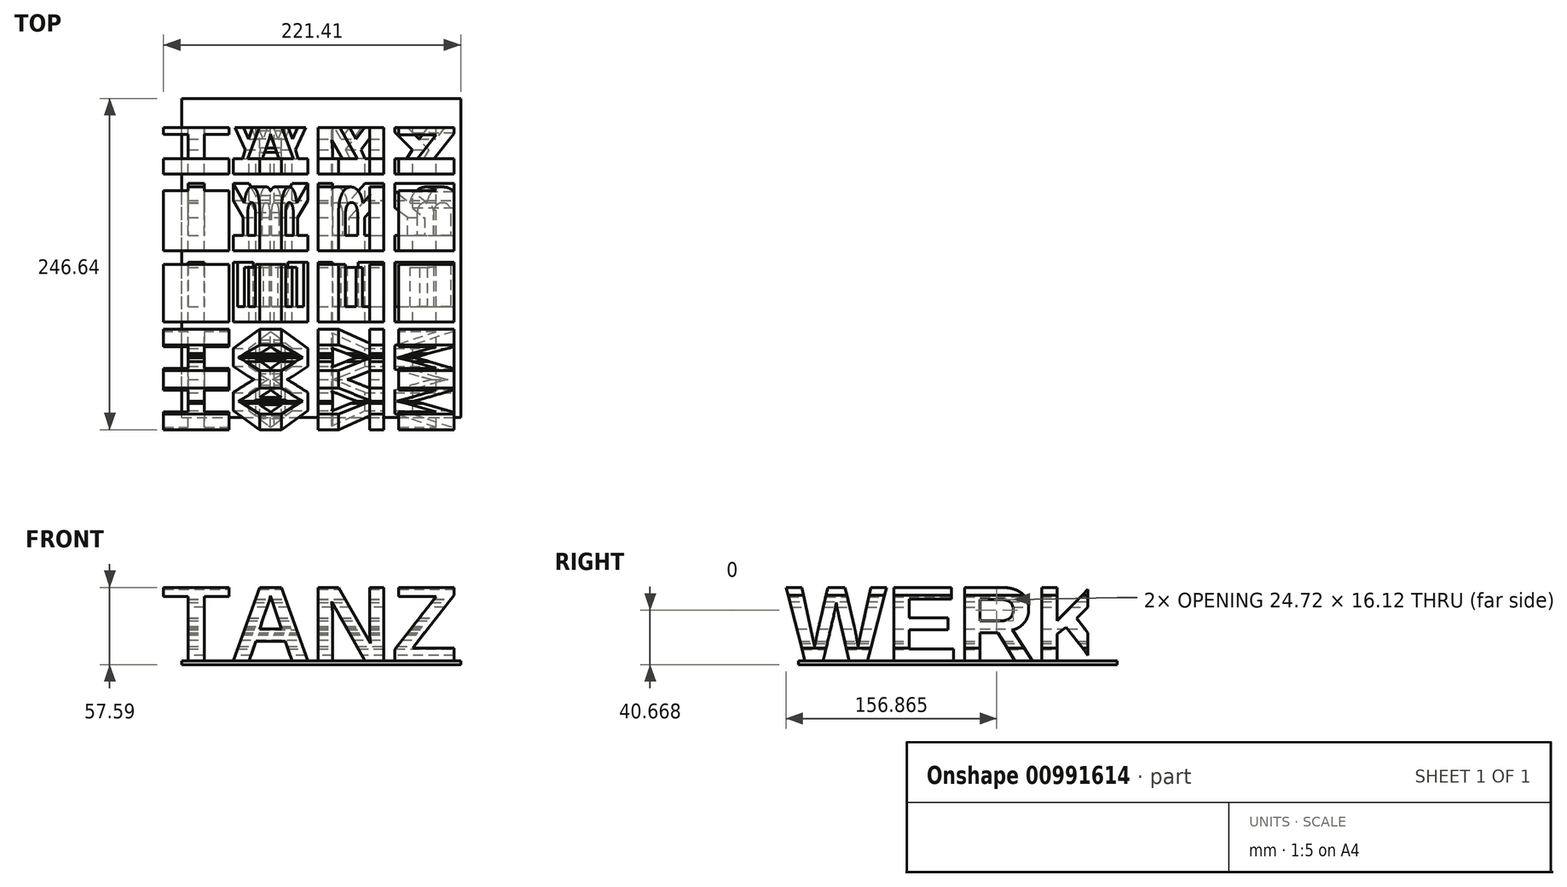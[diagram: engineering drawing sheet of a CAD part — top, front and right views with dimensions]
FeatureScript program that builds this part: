
annotation { "Feature Type Name" : "Feature", "Feature Type Description" : "" }
export const myFeature = defineFeature(function(context is Context, id is Id, definition is map)
    precondition{}
    {
        {
            var Q0;
            Q0=qCreatedBy(makeId("Front.planeOp"),FACE);
            var sketch = newSketch(context, id + "F0", { "sketchPlane" : qUnion([Q0])});
            skText(sketch, "E0", { "text": "TANZ", "fontName": "Arimo-Bold.ttf"});
            const initialGuessF0  = {"E0": [-0.14984, 0, 1, 0, 0.03986]};
            skSetInitialGuess(sketch, initialGuessF0);
            skSolve(sketch);
        }
        {
            var Q0;
            Q0 = qSketchRegion(id + "F0", true);
            extrude(context, id + "F1", {"entities" : qUnion([Q0]), "depth" : 164.8 * mm, "offsetDistance" : 25 * mm});
        }
        {
            var Q0;
            Q0=makeQuery(id+"F1.opExtrude","SWEPT_FACE",FACE,{"disambiguationData":[OSD([sQuery(id+"F0.wireOp",EDGE,"E0.sketch_text.stroke-41")])]});
            var sketch = newSketch(context, id + "F2", { "sketchPlane" : qUnion([Q0])});
            skPoint(sketch, "E1.0", {"position": v(-164.8, 38.09) * mm});
            skPoint(sketch, "E2.0", {"position": v(0, 0) * mm});
            skText(sketch, "E3", { "text": "WERK", "fontName": "Arimo-Bold.ttf"});
            const initialGuessF2  = {"E3": [-0.15, 0, 1, 0, 0.03809]};
            skSetInitialGuess(sketch, initialGuessF2);
            skSolve(sketch);
        }
        {
            var Q0;
            Q0 = qSketchRegion(id + "F2", true);
            extrude(context, id + "F3", {"entities" : qUnion([Q0]), "operationType" : NewBodyOperationType.INTERSECT, "endBound" : BoundingType.THROUGH_ALL, "oppositeDirection" : true, "depth" : 25 * mm, "offsetDistance" : 25 * mm});
        }
        {
            var Q0;
            Q0=makeQuery(id+"F3.boolean.opBoolean","SPLIT",BODY,{"disambiguationData":[OD(0.0)],"derivedFrom":makeQuery(id+"F1.opExtrude","SWEPT_BODY",BODY,{"disambiguationData":[OSD([sQuery(id+"F0.wireOp",EDGE,"E0.sketch_text.stroke-0"),sQuery(id+"F0.wireOp",EDGE,"E0.sketch_text.stroke-1"),sQuery(id+"F0.wireOp",EDGE,"E0.sketch_text.stroke-2"),sQuery(id+"F0.wireOp",EDGE,"E0.sketch_text.stroke-3"),sQuery(id+"F0.wireOp",EDGE,"E0.sketch_text.stroke-4"),sQuery(id+"F0.wireOp",EDGE,"E0.sketch_text.stroke-5"),sQuery(id+"F0.wireOp",EDGE,"E0.sketch_text.stroke-6"),sQuery(id+"F0.wireOp",EDGE,"E0.sketch_text.stroke-7")])]})});
            var Q1;
            Q1=makeQuery(id+"F3.boolean.opBoolean","SPLIT",BODY,{"disambiguationData":[OD(1.0)],"derivedFrom":makeQuery(id+"F1.opExtrude","SWEPT_BODY",BODY,{"disambiguationData":[OSD([sQuery(id+"F0.wireOp",EDGE,"E0.sketch_text.stroke-0"),sQuery(id+"F0.wireOp",EDGE,"E0.sketch_text.stroke-1"),sQuery(id+"F0.wireOp",EDGE,"E0.sketch_text.stroke-2"),sQuery(id+"F0.wireOp",EDGE,"E0.sketch_text.stroke-3"),sQuery(id+"F0.wireOp",EDGE,"E0.sketch_text.stroke-4"),sQuery(id+"F0.wireOp",EDGE,"E0.sketch_text.stroke-5"),sQuery(id+"F0.wireOp",EDGE,"E0.sketch_text.stroke-6"),sQuery(id+"F0.wireOp",EDGE,"E0.sketch_text.stroke-7")])]})});
            var Q2;
            Q2=makeQuery(id+"F3.boolean.opBoolean","SPLIT",BODY,{"disambiguationData":[OD(2.0)],"derivedFrom":makeQuery(id+"F1.opExtrude","SWEPT_BODY",BODY,{"disambiguationData":[OSD([sQuery(id+"F0.wireOp",EDGE,"E0.sketch_text.stroke-0"),sQuery(id+"F0.wireOp",EDGE,"E0.sketch_text.stroke-1"),sQuery(id+"F0.wireOp",EDGE,"E0.sketch_text.stroke-2"),sQuery(id+"F0.wireOp",EDGE,"E0.sketch_text.stroke-3"),sQuery(id+"F0.wireOp",EDGE,"E0.sketch_text.stroke-4"),sQuery(id+"F0.wireOp",EDGE,"E0.sketch_text.stroke-5"),sQuery(id+"F0.wireOp",EDGE,"E0.sketch_text.stroke-6"),sQuery(id+"F0.wireOp",EDGE,"E0.sketch_text.stroke-7")])]})});
            var Q3;
            Q3=makeQuery(id+"F3.boolean.opBoolean","SPLIT",BODY,{"disambiguationData":[OD(3.0)],"derivedFrom":makeQuery(id+"F1.opExtrude","SWEPT_BODY",BODY,{"disambiguationData":[OSD([sQuery(id+"F0.wireOp",EDGE,"E0.sketch_text.stroke-0"),sQuery(id+"F0.wireOp",EDGE,"E0.sketch_text.stroke-1"),sQuery(id+"F0.wireOp",EDGE,"E0.sketch_text.stroke-2"),sQuery(id+"F0.wireOp",EDGE,"E0.sketch_text.stroke-3"),sQuery(id+"F0.wireOp",EDGE,"E0.sketch_text.stroke-4"),sQuery(id+"F0.wireOp",EDGE,"E0.sketch_text.stroke-5"),sQuery(id+"F0.wireOp",EDGE,"E0.sketch_text.stroke-6"),sQuery(id+"F0.wireOp",EDGE,"E0.sketch_text.stroke-7")])]})});
            var Q4;
            Q4=makeQuery(id+"F3.boolean.opBoolean","SPLIT",BODY,{"disambiguationData":[OD(0.0)],"derivedFrom":makeQuery(id+"F1.opExtrude","SWEPT_BODY",BODY,{"disambiguationData":[OSD([sQuery(id+"F0.wireOp",EDGE,"E0.sketch_text.stroke-8"),sQuery(id+"F0.wireOp",EDGE,"E0.sketch_text.stroke-9"),sQuery(id+"F0.wireOp",EDGE,"E0.sketch_text.stroke-10"),sQuery(id+"F0.wireOp",EDGE,"E0.sketch_text.stroke-11"),sQuery(id+"F0.wireOp",EDGE,"E0.sketch_text.stroke-12"),sQuery(id+"F0.wireOp",EDGE,"E0.sketch_text.stroke-13"),sQuery(id+"F0.wireOp",EDGE,"E0.sketch_text.stroke-14"),sQuery(id+"F0.wireOp",EDGE,"E0.sketch_text.stroke-15"),sQuery(id+"F0.wireOp",EDGE,"E0.sketch_text.stroke-16"),sQuery(id+"F0.wireOp",EDGE,"E0.sketch_text.stroke-17"),sQuery(id+"F0.wireOp",EDGE,"E0.sketch_text.stroke-18"),sQuery(id+"F0.wireOp",EDGE,"E0.sketch_text.stroke-19"),sQuery(id+"F0.wireOp",EDGE,"E0.sketch_text.stroke-20"),sQuery(id+"F0.wireOp",EDGE,"E0.sketch_text.stroke-21"),sQuery(id+"F0.wireOp",EDGE,"E0.sketch_text.stroke-22")])]})});
            var Q5;
            Q5=makeQuery(id+"F3.boolean.opBoolean","SPLIT",BODY,{"disambiguationData":[OD(1.0)],"derivedFrom":makeQuery(id+"F1.opExtrude","SWEPT_BODY",BODY,{"disambiguationData":[OSD([sQuery(id+"F0.wireOp",EDGE,"E0.sketch_text.stroke-8"),sQuery(id+"F0.wireOp",EDGE,"E0.sketch_text.stroke-9"),sQuery(id+"F0.wireOp",EDGE,"E0.sketch_text.stroke-10"),sQuery(id+"F0.wireOp",EDGE,"E0.sketch_text.stroke-11"),sQuery(id+"F0.wireOp",EDGE,"E0.sketch_text.stroke-12"),sQuery(id+"F0.wireOp",EDGE,"E0.sketch_text.stroke-13"),sQuery(id+"F0.wireOp",EDGE,"E0.sketch_text.stroke-14"),sQuery(id+"F0.wireOp",EDGE,"E0.sketch_text.stroke-15"),sQuery(id+"F0.wireOp",EDGE,"E0.sketch_text.stroke-16"),sQuery(id+"F0.wireOp",EDGE,"E0.sketch_text.stroke-17"),sQuery(id+"F0.wireOp",EDGE,"E0.sketch_text.stroke-18"),sQuery(id+"F0.wireOp",EDGE,"E0.sketch_text.stroke-19"),sQuery(id+"F0.wireOp",EDGE,"E0.sketch_text.stroke-20"),sQuery(id+"F0.wireOp",EDGE,"E0.sketch_text.stroke-21"),sQuery(id+"F0.wireOp",EDGE,"E0.sketch_text.stroke-22")])]})});
            var Q6;
            Q6=makeQuery(id+"F3.boolean.opBoolean","SPLIT",BODY,{"disambiguationData":[OD(2.0)],"derivedFrom":makeQuery(id+"F1.opExtrude","SWEPT_BODY",BODY,{"disambiguationData":[OSD([sQuery(id+"F0.wireOp",EDGE,"E0.sketch_text.stroke-8"),sQuery(id+"F0.wireOp",EDGE,"E0.sketch_text.stroke-9"),sQuery(id+"F0.wireOp",EDGE,"E0.sketch_text.stroke-10"),sQuery(id+"F0.wireOp",EDGE,"E0.sketch_text.stroke-11"),sQuery(id+"F0.wireOp",EDGE,"E0.sketch_text.stroke-12"),sQuery(id+"F0.wireOp",EDGE,"E0.sketch_text.stroke-13"),sQuery(id+"F0.wireOp",EDGE,"E0.sketch_text.stroke-14"),sQuery(id+"F0.wireOp",EDGE,"E0.sketch_text.stroke-15"),sQuery(id+"F0.wireOp",EDGE,"E0.sketch_text.stroke-16"),sQuery(id+"F0.wireOp",EDGE,"E0.sketch_text.stroke-17"),sQuery(id+"F0.wireOp",EDGE,"E0.sketch_text.stroke-18"),sQuery(id+"F0.wireOp",EDGE,"E0.sketch_text.stroke-19"),sQuery(id+"F0.wireOp",EDGE,"E0.sketch_text.stroke-20"),sQuery(id+"F0.wireOp",EDGE,"E0.sketch_text.stroke-21"),sQuery(id+"F0.wireOp",EDGE,"E0.sketch_text.stroke-22")])]})});
            var Q7;
            Q7=makeQuery(id+"F3.boolean.opBoolean","SPLIT",BODY,{"disambiguationData":[OD(3.0)],"derivedFrom":makeQuery(id+"F1.opExtrude","SWEPT_BODY",BODY,{"disambiguationData":[OSD([sQuery(id+"F0.wireOp",EDGE,"E0.sketch_text.stroke-8"),sQuery(id+"F0.wireOp",EDGE,"E0.sketch_text.stroke-9"),sQuery(id+"F0.wireOp",EDGE,"E0.sketch_text.stroke-10"),sQuery(id+"F0.wireOp",EDGE,"E0.sketch_text.stroke-11"),sQuery(id+"F0.wireOp",EDGE,"E0.sketch_text.stroke-12"),sQuery(id+"F0.wireOp",EDGE,"E0.sketch_text.stroke-13"),sQuery(id+"F0.wireOp",EDGE,"E0.sketch_text.stroke-14"),sQuery(id+"F0.wireOp",EDGE,"E0.sketch_text.stroke-15"),sQuery(id+"F0.wireOp",EDGE,"E0.sketch_text.stroke-16"),sQuery(id+"F0.wireOp",EDGE,"E0.sketch_text.stroke-17"),sQuery(id+"F0.wireOp",EDGE,"E0.sketch_text.stroke-18"),sQuery(id+"F0.wireOp",EDGE,"E0.sketch_text.stroke-19"),sQuery(id+"F0.wireOp",EDGE,"E0.sketch_text.stroke-20"),sQuery(id+"F0.wireOp",EDGE,"E0.sketch_text.stroke-21"),sQuery(id+"F0.wireOp",EDGE,"E0.sketch_text.stroke-22")])]})});
            var Q8;
            Q8=makeQuery(id+"F3.boolean.opBoolean","SPLIT",BODY,{"disambiguationData":[OD(0.0)],"derivedFrom":makeQuery(id+"F1.opExtrude","SWEPT_BODY",BODY,{"disambiguationData":[OSD([sQuery(id+"F0.wireOp",EDGE,"E0.sketch_text.stroke-23"),sQuery(id+"F0.wireOp",EDGE,"E0.sketch_text.stroke-24"),sQuery(id+"F0.wireOp",EDGE,"E0.sketch_text.stroke-25"),sQuery(id+"F0.wireOp",EDGE,"E0.sketch_text.stroke-26"),sQuery(id+"F0.wireOp",EDGE,"E0.sketch_text.stroke-27"),sQuery(id+"F0.wireOp",EDGE,"E0.sketch_text.stroke-28"),sQuery(id+"F0.wireOp",EDGE,"E0.sketch_text.stroke-29"),sQuery(id+"F0.wireOp",EDGE,"E0.sketch_text.stroke-30"),sQuery(id+"F0.wireOp",EDGE,"E0.sketch_text.stroke-31"),sQuery(id+"F0.wireOp",EDGE,"E0.sketch_text.stroke-32"),sQuery(id+"F0.wireOp",EDGE,"E0.sketch_text.stroke-33"),sQuery(id+"F0.wireOp",EDGE,"E0.sketch_text.stroke-34")])]})});
            var Q9;
            Q9=makeQuery(id+"F3.boolean.opBoolean","SPLIT",BODY,{"disambiguationData":[OD(1.0)],"derivedFrom":makeQuery(id+"F1.opExtrude","SWEPT_BODY",BODY,{"disambiguationData":[OSD([sQuery(id+"F0.wireOp",EDGE,"E0.sketch_text.stroke-23"),sQuery(id+"F0.wireOp",EDGE,"E0.sketch_text.stroke-24"),sQuery(id+"F0.wireOp",EDGE,"E0.sketch_text.stroke-25"),sQuery(id+"F0.wireOp",EDGE,"E0.sketch_text.stroke-26"),sQuery(id+"F0.wireOp",EDGE,"E0.sketch_text.stroke-27"),sQuery(id+"F0.wireOp",EDGE,"E0.sketch_text.stroke-28"),sQuery(id+"F0.wireOp",EDGE,"E0.sketch_text.stroke-29"),sQuery(id+"F0.wireOp",EDGE,"E0.sketch_text.stroke-30"),sQuery(id+"F0.wireOp",EDGE,"E0.sketch_text.stroke-31"),sQuery(id+"F0.wireOp",EDGE,"E0.sketch_text.stroke-32"),sQuery(id+"F0.wireOp",EDGE,"E0.sketch_text.stroke-33"),sQuery(id+"F0.wireOp",EDGE,"E0.sketch_text.stroke-34")])]})});
            var Q10;
            Q10=makeQuery(id+"F3.boolean.opBoolean","SPLIT",BODY,{"disambiguationData":[OD(0.0)],"derivedFrom":makeQuery(id+"F1.opExtrude","SWEPT_BODY",BODY,{"disambiguationData":[OSD([sQuery(id+"F0.wireOp",EDGE,"E0.sketch_text.stroke-35"),sQuery(id+"F0.wireOp",EDGE,"E0.sketch_text.stroke-36"),sQuery(id+"F0.wireOp",EDGE,"E0.sketch_text.stroke-37"),sQuery(id+"F0.wireOp",EDGE,"E0.sketch_text.stroke-38"),sQuery(id+"F0.wireOp",EDGE,"E0.sketch_text.stroke-39"),sQuery(id+"F0.wireOp",EDGE,"E0.sketch_text.stroke-40"),sQuery(id+"F0.wireOp",EDGE,"E0.sketch_text.stroke-41"),sQuery(id+"F0.wireOp",EDGE,"E0.sketch_text.stroke-42"),sQuery(id+"F0.wireOp",EDGE,"E0.sketch_text.stroke-43"),sQuery(id+"F0.wireOp",EDGE,"E0.sketch_text.stroke-44")])]})});
            var Q11;
            Q11=makeQuery(id+"F3.boolean.opBoolean","SPLIT",BODY,{"disambiguationData":[OD(1.0)],"derivedFrom":makeQuery(id+"F1.opExtrude","SWEPT_BODY",BODY,{"disambiguationData":[OSD([sQuery(id+"F0.wireOp",EDGE,"E0.sketch_text.stroke-35"),sQuery(id+"F0.wireOp",EDGE,"E0.sketch_text.stroke-36"),sQuery(id+"F0.wireOp",EDGE,"E0.sketch_text.stroke-37"),sQuery(id+"F0.wireOp",EDGE,"E0.sketch_text.stroke-38"),sQuery(id+"F0.wireOp",EDGE,"E0.sketch_text.stroke-39"),sQuery(id+"F0.wireOp",EDGE,"E0.sketch_text.stroke-40"),sQuery(id+"F0.wireOp",EDGE,"E0.sketch_text.stroke-41"),sQuery(id+"F0.wireOp",EDGE,"E0.sketch_text.stroke-42"),sQuery(id+"F0.wireOp",EDGE,"E0.sketch_text.stroke-43"),sQuery(id+"F0.wireOp",EDGE,"E0.sketch_text.stroke-44")])]})});
            var Q12;
            Q12=makeQuery(id+"F3.boolean.opBoolean","SPLIT",BODY,{"disambiguationData":[OD(2.0)],"derivedFrom":makeQuery(id+"F1.opExtrude","SWEPT_BODY",BODY,{"disambiguationData":[OSD([sQuery(id+"F0.wireOp",EDGE,"E0.sketch_text.stroke-35"),sQuery(id+"F0.wireOp",EDGE,"E0.sketch_text.stroke-36"),sQuery(id+"F0.wireOp",EDGE,"E0.sketch_text.stroke-37"),sQuery(id+"F0.wireOp",EDGE,"E0.sketch_text.stroke-38"),sQuery(id+"F0.wireOp",EDGE,"E0.sketch_text.stroke-39"),sQuery(id+"F0.wireOp",EDGE,"E0.sketch_text.stroke-40"),sQuery(id+"F0.wireOp",EDGE,"E0.sketch_text.stroke-41"),sQuery(id+"F0.wireOp",EDGE,"E0.sketch_text.stroke-42"),sQuery(id+"F0.wireOp",EDGE,"E0.sketch_text.stroke-43"),sQuery(id+"F0.wireOp",EDGE,"E0.sketch_text.stroke-44")])]})});
            var Q13;
            Q13=makeQuery(id+"F3.boolean.opBoolean","SPLIT",BODY,{"disambiguationData":[OD(3.0)],"derivedFrom":makeQuery(id+"F1.opExtrude","SWEPT_BODY",BODY,{"disambiguationData":[OSD([sQuery(id+"F0.wireOp",EDGE,"E0.sketch_text.stroke-35"),sQuery(id+"F0.wireOp",EDGE,"E0.sketch_text.stroke-36"),sQuery(id+"F0.wireOp",EDGE,"E0.sketch_text.stroke-37"),sQuery(id+"F0.wireOp",EDGE,"E0.sketch_text.stroke-38"),sQuery(id+"F0.wireOp",EDGE,"E0.sketch_text.stroke-39"),sQuery(id+"F0.wireOp",EDGE,"E0.sketch_text.stroke-40"),sQuery(id+"F0.wireOp",EDGE,"E0.sketch_text.stroke-41"),sQuery(id+"F0.wireOp",EDGE,"E0.sketch_text.stroke-42"),sQuery(id+"F0.wireOp",EDGE,"E0.sketch_text.stroke-43"),sQuery(id+"F0.wireOp",EDGE,"E0.sketch_text.stroke-44")])]})});
            var Q14;
            Q14=makeQuery(id+"F3.boolean.opBoolean","SPLIT",BODY,{"disambiguationData":[OD(2.0)],"derivedFrom":makeQuery(id+"F1.opExtrude","SWEPT_BODY",BODY,{"disambiguationData":[OSD([sQuery(id+"F0.wireOp",EDGE,"E0.sketch_text.stroke-23"),sQuery(id+"F0.wireOp",EDGE,"E0.sketch_text.stroke-24"),sQuery(id+"F0.wireOp",EDGE,"E0.sketch_text.stroke-25"),sQuery(id+"F0.wireOp",EDGE,"E0.sketch_text.stroke-26"),sQuery(id+"F0.wireOp",EDGE,"E0.sketch_text.stroke-27"),sQuery(id+"F0.wireOp",EDGE,"E0.sketch_text.stroke-28"),sQuery(id+"F0.wireOp",EDGE,"E0.sketch_text.stroke-29"),sQuery(id+"F0.wireOp",EDGE,"E0.sketch_text.stroke-30"),sQuery(id+"F0.wireOp",EDGE,"E0.sketch_text.stroke-31"),sQuery(id+"F0.wireOp",EDGE,"E0.sketch_text.stroke-32"),sQuery(id+"F0.wireOp",EDGE,"E0.sketch_text.stroke-33"),sQuery(id+"F0.wireOp",EDGE,"E0.sketch_text.stroke-34")])]})});
            var Q15;
            Q15=makeQuery(id+"F3.boolean.opBoolean","SPLIT",BODY,{"disambiguationData":[OD(3.0)],"derivedFrom":makeQuery(id+"F1.opExtrude","SWEPT_BODY",BODY,{"disambiguationData":[OSD([sQuery(id+"F0.wireOp",EDGE,"E0.sketch_text.stroke-23"),sQuery(id+"F0.wireOp",EDGE,"E0.sketch_text.stroke-24"),sQuery(id+"F0.wireOp",EDGE,"E0.sketch_text.stroke-25"),sQuery(id+"F0.wireOp",EDGE,"E0.sketch_text.stroke-26"),sQuery(id+"F0.wireOp",EDGE,"E0.sketch_text.stroke-27"),sQuery(id+"F0.wireOp",EDGE,"E0.sketch_text.stroke-28"),sQuery(id+"F0.wireOp",EDGE,"E0.sketch_text.stroke-29"),sQuery(id+"F0.wireOp",EDGE,"E0.sketch_text.stroke-30"),sQuery(id+"F0.wireOp",EDGE,"E0.sketch_text.stroke-31"),sQuery(id+"F0.wireOp",EDGE,"E0.sketch_text.stroke-32"),sQuery(id+"F0.wireOp",EDGE,"E0.sketch_text.stroke-33"),sQuery(id+"F0.wireOp",EDGE,"E0.sketch_text.stroke-34")])]})});
            var Q16;
            Q16=qCreatedBy(makeId("Origin.pointOp"),VERTEX);
            transform(context, id + "F4", {"entities" : qUnion([Q0, Q1, Q2, Q3, Q4, Q5, Q6, Q7, Q8, Q9, Q10, Q11, Q12, Q13, Q14, Q15]), "transformType" : TransformType.SCALE_UNIFORMLY, "scale" : 1.5, "scalePoint" : qUnion([Q16]), "makeCopy" : false});
        }
        {
            var Q0;
            Q0=qCreatedBy(makeId("Top.planeOp"),FACE);
            var sketch = newSketch(context, id + "F5", { "sketchPlane" : qUnion([Q0])});
            skPoint(sketch, "E4.0", {"position": v(-223.83, -224.93) * mm});
            skPoint(sketch, "E5.0", {"position": v(-7.42, 16.7) * mm});
            skLineSegment(sketch, "E6.bottom", {"start": v(-223.83, -224.93) * mm, "end": v(-7.42, -224.93) * mm, "construction": true});
            skLineSegment(sketch, "E6.top", {"start": v(-223.83, 16.7) * mm, "end": v(-7.42, 16.7) * mm, "construction": true});
            skLineSegment(sketch, "E6.left", {"start": v(-223.83, -224.93) * mm, "end": v(-223.83, 16.7) * mm, "construction": true});
            skLineSegment(sketch, "E6.right", {"start": v(-7.42, -224.93) * mm, "end": v(-7.42, 16.7) * mm, "construction": true});
            skLineSegment(sketch, "E7.bottom", {"start": v(-210.38, -215.85) * mm, "end": v(-2.42, -215.85) * mm});
            skLineSegment(sketch, "E7.top", {"start": v(-210.38, 21.7) * mm, "end": v(-2.42, 21.7) * mm});
            skLineSegment(sketch, "E7.left", {"start": v(-210.38, -215.85) * mm, "end": v(-210.38, 21.7) * mm});
            skLineSegment(sketch, "E7.right", {"start": v(-2.42, -215.85) * mm, "end": v(-2.42, 21.7) * mm});
            skLineSegment(sketch, "E8.0", {"start": v(-205.38, -210.85) * mm, "end": v(-193.42, -210.85) * mm, "construction": true});
            skLineSegment(sketch, "E9.0", {"start": v(-205.38, -144.8) * mm, "end": v(-205.38, -100.27) * mm, "construction": true});
            skSolve(sketch);
        }
        {
            var Q0;
            Q0 = qSketchRegion(id + "F5", true);
            extrude(context, id + "F6", {"entities" : qUnion([Q0]), "operationType" : NewBodyOperationType.ADD, "oppositeDirection" : true, "depth" : 3 * mm, "offsetDistance" : 25 * mm});
        }
    });
